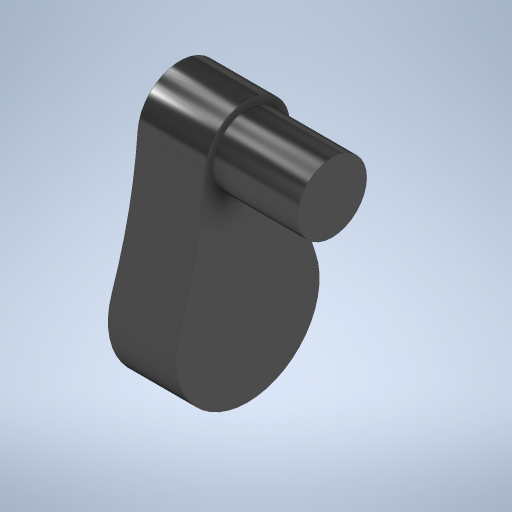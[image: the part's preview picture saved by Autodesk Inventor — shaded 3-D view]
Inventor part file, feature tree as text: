
AUTODESK INVENTOR PART (.ipt)
format: ipt  version: 2023 (Build 270158000, 158)  size: 275,456 bytes
history: native  units: mm
features: extrude x3, sketch x3
ambient origin geometry x8: Origin, YZ Plane, XZ Plane, XY Plane, X Axis, Y Axis, Z Axis, Center Point
bodies: Volumenkörper1 (feature_tree)
feature tree (6):
  extrude  "Extrusion1"  Depth=10.0mm
  extrude  "Extrusion2"  Depth=60.0mm
  extrude  "Extrusion4"  TaperAngle=0.0deg  [1 undecoded]
  sketch  "Skizze1"  dims[d0=10.0mm d1=17.0mm]
  sketch  "Skizze2"  dims[d2=17.5mm d3=60.0mm]
  sketch  "Skizze4"  dims[d4=0.0mm d5=0.0mm d6=60.0mm d7=8.0mm d8=0.0mm d9=8.2mm d10=10.0mm d11=0.0mm d15=12.1mm d16=6.0mm d17=0.0mm]
note: 1 required parameter value undecoded (feature->parameter linkage not recoverable at this tier; creation-order binding heuristic only, values carry confidence <= 0.55)
